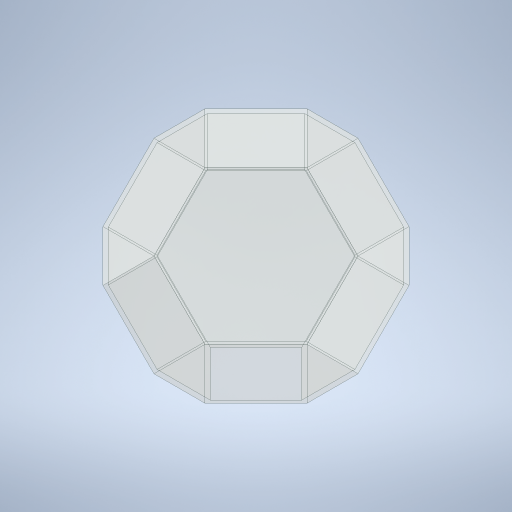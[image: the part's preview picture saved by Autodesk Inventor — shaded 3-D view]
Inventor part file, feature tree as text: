
AUTODESK INVENTOR PART (.ipt)
format: ipt  version: 2024 (Build 280153000, 153)  size: 295,424 bytes
history: native  units: in
note: dims shown in document units (in); Inventor stores cm internally (conversion verified against a paired STEP export)
features: other x6, pattern_circular x3, extrude x2, sketch x2, plane x1, shell x1
ambient origin geometry x8: Origin, YZ Plane, XZ Plane, XY Plane, X Axis, Y Axis, Z Axis, Center Point
bodies: Body1 (feature_tree)
feature tree (15):
  extrude  "Extrusion9"  Depth=4.5961in
  pattern_circular  "Circular Pattern14"  [2 undecoded]
  pattern_circular  "Circular Pattern15"  [2 undecoded]
  plane  "Work Plane9"
  extrude  "Extrusion10"  Depth=0.1969in TaperAngle=360.0deg
  pattern_circular  "Circular Pattern16"  Count=4 Angle=360.0deg
  shell  "Shell2"  Thickness=12.9996in
  sketch  "Sketch26"  dims[d65=13.6386in d75=8.1268in d97=4.5961in]
  other  "Work Axis1"
  other  "Work Axis2"
  other  "Work Axis3"
  other  "Work Axis4"
  other  "Work Axis5"
  other  "Work Axis6"
  sketch  "Sketch27"  dims[d98=6.4998in d99=12.9996in d100=0.0in d101=1.5748in d102=360.0deg d104=1.5748in d105=360.0deg d107=12.9996in d108=0.0in d109=1.5748in d110=360.0deg d112=0.1969in d88=0.1969in d89=0.0344in d90=0.1969in d91=0.0344in d92=0.1969in d93=0.0344in]
note: 4 required parameter values undecoded (feature->parameter linkage not recoverable at this tier; creation-order binding heuristic only, values carry confidence <= 0.55)
